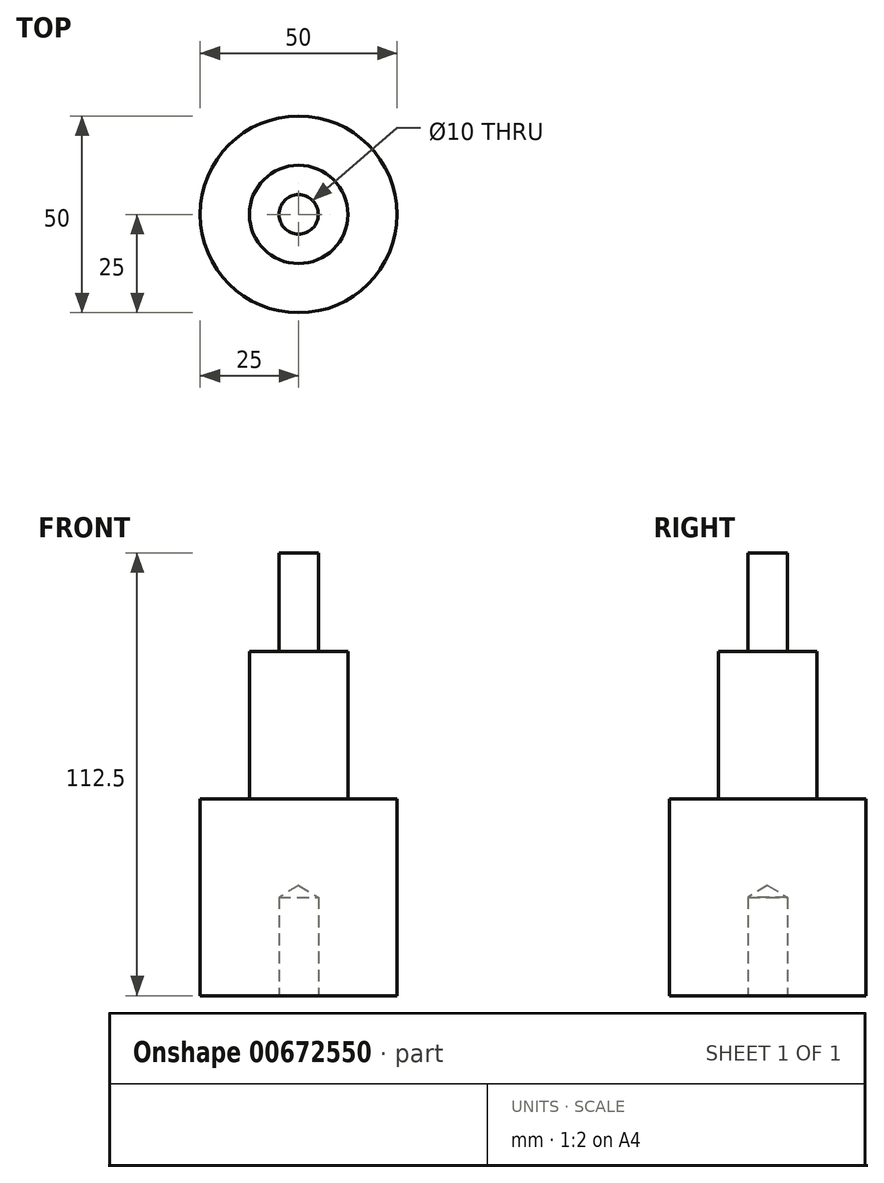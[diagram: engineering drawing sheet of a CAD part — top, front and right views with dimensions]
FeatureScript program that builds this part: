
annotation { "Feature Type Name" : "Feature", "Feature Type Description" : "" }
export const myFeature = defineFeature(function(context is Context, id is Id, definition is map)
    precondition{}
    {
        {
            var Q0;
            Q0=qCreatedBy(makeId("Top.planeOp"),FACE);
            var sketch = newSketch(context, id + "F0", { "sketchPlane" : qUnion([Q0])});
            skCircle(sketch, "E0", {"center": v(0, 0) * mm, "radius": 25 * mm});
            skSolve(sketch);
        }
        {
            var Q0;
            Q0=makeQuery(id+"F0.imprint","IMPRINT",FACE,{"disambiguationData":[TD([[makeQuery(id+"F0.imprint","IMPRINT",EDGE,{"derivedFrom":sQuery(id+"F0.wireOp",EDGE,"E0")}),1.0]])]});
            var sketch = newSketch(context, id + "F1", { "sketchPlane" : qUnion([Q0])});
            skSolve(sketch);
        }
        {
            var Q0;
            Q0=makeQuery(id+"F0.imprint","IMPRINT",FACE,{"disambiguationData":[TD([[makeQuery(id+"F0.imprint","IMPRINT",EDGE,{"derivedFrom":sQuery(id+"F0.wireOp",EDGE,"E0")}),1.0]])]});
            extrude(context, id + "F2", {"entities" : qUnion([Q0]), "depth" : 50 * mm, "offsetDistance" : 25.4 * mm});
        }
        {
            var Q0;
            Q0=makeQuery(id+"F2.opExtrude","CAP_FACE",FACE,{"disambiguationData":[OSD([sQuery(id+"F0.wireOp",EDGE,"E0")])],"isStart":false});
            var sketch = newSketch(context, id + "F3", { "sketchPlane" : qUnion([Q0])});
            skCircle(sketch, "E1", {"center": v(0, 0) * mm, "radius": 12.5 * mm});
            skSolve(sketch);
        }
        {
            var Q0;
            Q0 = qSketchRegion(id + "F3", true);
            var Q1;
            Q1=makeQuery(id+"F3.imprint","IMPRINT",FACE,{"disambiguationData":[TD([[makeQuery(id+"F3.imprint","IMPRINT",EDGE,{"derivedFrom":sQuery(id+"F3.wireOp",EDGE,"E1")}),1.0]])]});
            extrude(context, id + "F4", {"entities" : qUnion([Q0, Q1]), "operationType" : NewBodyOperationType.ADD, "depth" : 37.5 * mm, "offsetDistance" : 25.4 * mm});
        }
        {
            var Q0;
            Q0=makeQuery(id+"FTgaLnHNsKb6wIb_1.opExtrude","CAP_FACE",FACE,{"disambiguationData":[OSD([sQuery(id+"F3JtwcCn2Gt3H76_1.wireOp",EDGE,"6bb3b38a-1615-435a-9ba9-54a1126218c2.bottom"),sQuery(id+"F3JtwcCn2Gt3H76_1.wireOp",EDGE,"6bb3b38a-1615-435a-9ba9-54a1126218c2.top"),sQuery(id+"F3JtwcCn2Gt3H76_1.wireOp",EDGE,"6bb3b38a-1615-435a-9ba9-54a1126218c2.left"),sQuery(id+"F3JtwcCn2Gt3H76_1.wireOp",EDGE,"6bb3b38a-1615-435a-9ba9-54a1126218c2.right")])],"isStart":false});
            var sketch = newSketch(context, id + "F5", { "sketchPlane" : qUnion([Q0])});
            skPoint(sketch, "E2", {"position": v(0, 0) * mm});
            skSolve(sketch);
        }
        {
            var Q0;
            Q0=makeQuery(id+"F1.imprint","IMPRINT",FACE,{"disambiguationData":[TD([[makeQuery(id+"F1.imprint","IMPRINT",EDGE,{"derivedFrom":makeQuery(id+"F0.imprint","IMPRINT",EDGE,{"derivedFrom":sQuery(id+"F0.wireOp",EDGE,"E0")})}),1.0]])]});
            var sketch = newSketch(context, id + "F6", { "sketchPlane" : qUnion([Q0])});
            skLineSegment(sketch, "E3.bottom", {"start": v(5, 5) * mm, "end": v(-5, 5) * mm});
            skLineSegment(sketch, "E3.top", {"start": v(5, -5) * mm, "end": v(-5, -5) * mm});
            skLineSegment(sketch, "E3.left", {"start": v(5, 5) * mm, "end": v(5, -5) * mm});
            skLineSegment(sketch, "E3.right", {"start": v(-5, 5) * mm, "end": v(-5, -5) * mm});
            skPoint(sketch, "E3.middle", {"position": v(0, 0) * mm});
            skSolve(sketch);
        }
        {
            var Q0;
            Q0=makeQuery(id+"F6.imprint","IMPRINT",FACE,{"disambiguationData":[TD([[makeQuery(id+"F6.imprint","IMPRINT",EDGE,{"derivedFrom":sQuery(id+"F6.wireOp",EDGE,"E3.bottom")}),1.0]])]});
            var sketch = newSketch(context, id + "F7", { "sketchPlane" : qUnion([Q0])});
            skSolve(sketch);
        }
        {
            var Q0;
            Q0=makeQuery(id+"F7.imprint","IMPRINT",FACE,{"disambiguationData":[TD([[makeQuery(id+"F7.imprint","IMPRINT",EDGE,{"derivedFrom":makeQuery(id+"F6.imprint","IMPRINT",EDGE,{"derivedFrom":sQuery(id+"F6.wireOp",EDGE,"E3.bottom")})}),1.0]])]});
            extrude(context, id + "F8", {"entities" : qUnion([Q0]), "operationType" : NewBodyOperationType.ADD, "depth" : 25 * mm, "offsetDistance" : 25.4 * mm});
        }
        {
            var Q0;
            Q0=makeQuery(id+"F1.imprint","IMPRINT",FACE,{"disambiguationData":[TD([[makeQuery(id+"F1.imprint","IMPRINT",EDGE,{"derivedFrom":makeQuery(id+"F0.imprint","IMPRINT",EDGE,{"derivedFrom":sQuery(id+"F0.wireOp",EDGE,"E0")})}),1.0]])]});
            var sketch = newSketch(context, id + "F9", { "sketchPlane" : qUnion([Q0])});
            skSolve(sketch);
        }
        {
            var Q0;
            Q0=sQuery(id+"F6.wireOp",VERTEX,"E3.middle");
            var Q1;
            Q1=makeQuery(id+"F2.opExtrude","SWEPT_BODY",BODY,{"disambiguationData":[OSD([sQuery(id+"F0.wireOp",EDGE,"E0")])]});
            hole(context, id + "F10", {"style" : HoleStyle.SIMPLE, "endStyle" : HoleEndStyle.BLIND, "oppositeDirection" : true, "holeDiameter" : 10 * mm, "majorDiameter" : 6.35 * mm, "holeDepth" : 25 * mm, "isTappedThrough" : true, "tappedDepth" : 12.7 * mm, "tapClearance" : 3, "locations" : qUnion([Q0]), "scope" : qUnion([Q1])});
        }
        {
            var Q0;
            Q0=makeQuery(id+"F4.opExtrude","CAP_FACE",FACE,{"disambiguationData":[OSD([sQuery(id+"F3.wireOp",EDGE,"E1")])],"isStart":false});
            var sketch = newSketch(context, id + "F11", { "sketchPlane" : qUnion([Q0])});
            skPoint(sketch, "E4", {"position": v(0, 0) * mm});
            skCircle(sketch, "E5", {"center": v(0, 0) * mm, "radius": 5 * mm});
            skSolve(sketch);
        }
        {
            var Q0;
            Q0=makeQuery(id+"F11.imprint","IMPRINT",FACE,{"disambiguationData":[TD([[makeQuery(id+"F11.imprint","IMPRINT",EDGE,{"derivedFrom":sQuery(id+"F11.wireOp",EDGE,"E5")}),1.0]])]});
            extrude(context, id + "F12", {"entities" : qUnion([Q0]), "operationType" : NewBodyOperationType.ADD, "depth" : 25 * mm, "offsetDistance" : 25.4 * mm});
        }
    });
